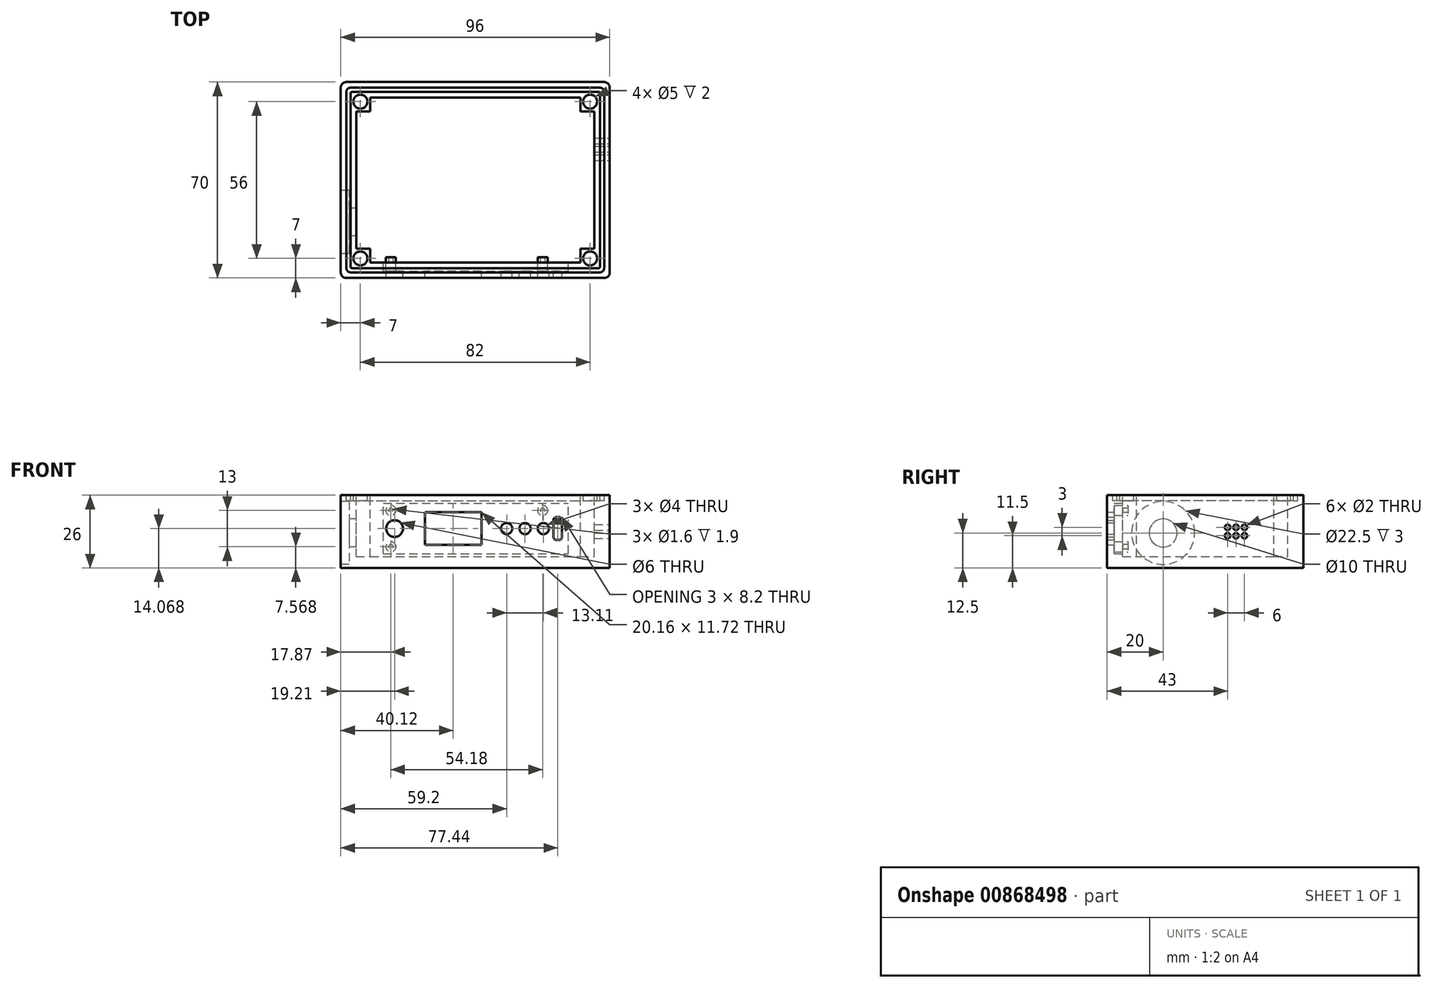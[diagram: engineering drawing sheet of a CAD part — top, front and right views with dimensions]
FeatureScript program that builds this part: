
annotation { "Feature Type Name" : "Feature", "Feature Type Description" : "" }
export const myFeature = defineFeature(function(context is Context, id is Id, definition is map)
    precondition{}
    {
        {
            var Q0;
            Q0=qCreatedBy(makeId("Top.planeOp"),FACE);
            var sketch = newSketch(context, id + "F0", { "sketchPlane" : qUnion([Q0])});
            skLineSegment(sketch, "E0.bottom", {"start": v(-46, 35) * mm, "end": v(46, 35) * mm});
            skLineSegment(sketch, "E0.top", {"start": v(-46, -35) * mm, "end": v(46, -35) * mm});
            skLineSegment(sketch, "E0.left", {"start": v(-48, 33) * mm, "end": v(-48, -33) * mm});
            skLineSegment(sketch, "E0.right", {"start": v(48, 33) * mm, "end": v(48, -33) * mm});
            skPoint(sketch, "E0.middle", {"position": v(0, 0) * mm});
            skPoint(sketch, "E1.visualSharp", {"position": v(-48, 35) * mm});
            skArc(sketch, "E1.filletArc", {"start": v(-46, 35) * mm, "mid": v(-47.41, 34.41) * mm, "end": v(-48, 33) * mm});
            skPoint(sketch, "E2.visualSharp", {"position": v(-48, -35) * mm});
            skArc(sketch, "E2.filletArc", {"start": v(-48, -33) * mm, "mid": v(-47.41, -34.41) * mm, "end": v(-46, -35) * mm});
            skPoint(sketch, "E3.visualSharp", {"position": v(48, -35) * mm});
            skArc(sketch, "E3.filletArc", {"start": v(46, -35) * mm, "mid": v(47.41, -34.41) * mm, "end": v(48, -33) * mm});
            skPoint(sketch, "E4.visualSharp", {"position": v(48, 35) * mm});
            skArc(sketch, "E4.filletArc", {"start": v(48, 33) * mm, "mid": v(47.41, 34.41) * mm, "end": v(46, 35) * mm});
            skSolve(sketch);
        }
        {
            var Q0;
            Q0=makeQuery(id+"F0.imprint","IMPRINT",FACE,{"disambiguationData":[TD([[makeQuery(id+"F0.imprint","IMPRINT",EDGE,{"derivedFrom":sQuery(id+"F0.wireOp",EDGE,"U18dfylj-Norm-gyCY-oxJm-QVkYRqjWbd2D.bottom")}),-1.0]])]});
            var Q1;
            Q1 = qSketchRegion(id + "F0", true);
            extrude(context, id + "F1", {"entities" : qUnion([Q0, Q1]), "depth" : 26 * mm, "offsetDistance" : 25 * mm});
        }
        {
            var Q0;
            Q0=makeQuery(id+"F1.opExtrude","CAP_FACE",FACE,{"disambiguationData":[OSD([sQuery(id+"F0.wireOp",EDGE,"E0.bottom"),sQuery(id+"F0.wireOp",EDGE,"E0.top"),sQuery(id+"F0.wireOp",EDGE,"E0.left"),sQuery(id+"F0.wireOp",EDGE,"E0.right"),sQuery(id+"F0.wireOp",EDGE,"E1.filletArc"),sQuery(id+"F0.wireOp",EDGE,"E2.filletArc"),sQuery(id+"F0.wireOp",EDGE,"E3.filletArc"),sQuery(id+"F0.wireOp",EDGE,"E4.filletArc")])],"isStart":false});
            var sketch = newSketch(context, id + "F2", { "sketchPlane" : qUnion([Q0])});
            skLineSegment(sketch, "E5.bottom", {"start": v(-44.5, 33) * mm, "end": v(44.5, 33) * mm});
            skLineSegment(sketch, "E5.top", {"start": v(-44.5, -33) * mm, "end": v(44.5, -33) * mm});
            skLineSegment(sketch, "E5.left", {"start": v(-46, 31.5) * mm, "end": v(-46, -31.5) * mm});
            skLineSegment(sketch, "E5.right", {"start": v(46, 31.5) * mm, "end": v(46, -31.5) * mm});
            skPoint(sketch, "E5.middle", {"position": v(0, 0) * mm});
            skPoint(sketch, "E6.visualSharp", {"position": v(-46, 33) * mm});
            skArc(sketch, "E6.filletArc", {"start": v(-44.5, 33) * mm, "mid": v(-45.56, 32.56) * mm, "end": v(-46, 31.5) * mm});
            skPoint(sketch, "E7.visualSharp", {"position": v(46, 33) * mm});
            skArc(sketch, "E7.filletArc", {"start": v(46, 31.5) * mm, "mid": v(45.56, 32.56) * mm, "end": v(44.5, 33) * mm});
            skPoint(sketch, "E8.visualSharp", {"position": v(46, -33) * mm});
            skArc(sketch, "E8.filletArc", {"start": v(44.5, -33) * mm, "mid": v(45.56, -32.56) * mm, "end": v(46, -31.5) * mm});
            skPoint(sketch, "E9.visualSharp", {"position": v(-46, -33) * mm});
            skArc(sketch, "E9.filletArc", {"start": v(-46, -31.5) * mm, "mid": v(-45.56, -32.56) * mm, "end": v(-44.5, -33) * mm});
            skLineSegment(sketch, "E10.bottom", {"start": v(-44, 31.5) * mm, "end": v(44, 31.5) * mm});
            skLineSegment(sketch, "E10.top", {"start": v(-44, -31.5) * mm, "end": v(44, -31.5) * mm});
            skLineSegment(sketch, "E10.left", {"start": v(-44.5, 31) * mm, "end": v(-44.5, -31) * mm});
            skLineSegment(sketch, "E10.right", {"start": v(44.5, 31) * mm, "end": v(44.5, -31) * mm});
            skArc(sketch, "E11.filletArc", {"start": v(-44, 31.5) * mm, "mid": v(-44.35, 31.35) * mm, "end": v(-44.5, 31) * mm});
            skArc(sketch, "E12.filletArc", {"start": v(-44.5, -31) * mm, "mid": v(-44.35, -31.35) * mm, "end": v(-44, -31.5) * mm});
            skArc(sketch, "E13.filletArc", {"start": v(44, -31.5) * mm, "mid": v(44.35, -31.35) * mm, "end": v(44.5, -31) * mm});
            skArc(sketch, "E14.filletArc", {"start": v(44.5, 31) * mm, "mid": v(44.35, 31.35) * mm, "end": v(44, 31.5) * mm});
            skSolve(sketch);
        }
        {
            var Q0;
            Q0=makeQuery(id+"F2.imprint","IMPRINT",FACE,{"disambiguationData":[TD([[makeQuery(id+"F2.imprint","IMPRINT",EDGE,{"derivedFrom":sQuery(id+"F2.wireOp",EDGE,"E5.bottom")}),-1.0]])]});
            extrude(context, id + "F3", {"entities" : qUnion([Q0]), "operationType" : NewBodyOperationType.REMOVE, "oppositeDirection" : true, "depth" : 2 * mm, "offsetDistance" : 25 * mm});
        }
        {
            var Q0;
            Q0=makeQuery(id+"F3.boolean.opBoolean","SPLIT",FACE,{"disambiguationData":[TD([makeQuery(id+"F3.opExtrude","SWEPT_FACE",FACE,{"disambiguationData":[OSD([sQuery(id+"F2.wireOp",EDGE,"E10.bottom")])]})])],"derivedFrom":makeQuery(id+"F1.opExtrude","CAP_FACE",FACE,{"disambiguationData":[OSD([sQuery(id+"F0.wireOp",EDGE,"E0.bottom"),sQuery(id+"F0.wireOp",EDGE,"E0.top"),sQuery(id+"F0.wireOp",EDGE,"E0.left"),sQuery(id+"F0.wireOp",EDGE,"E0.right"),sQuery(id+"F0.wireOp",EDGE,"E1.filletArc"),sQuery(id+"F0.wireOp",EDGE,"E2.filletArc"),sQuery(id+"F0.wireOp",EDGE,"E3.filletArc"),sQuery(id+"F0.wireOp",EDGE,"E4.filletArc")])],"isStart":false})});
            var sketch = newSketch(context, id + "F4", { "sketchPlane" : qUnion([Q0])});
            skCircle(sketch, "E15", {"center": v(-41, -28) * mm, "radius": 2.5 * mm});
            skCircle(sketch, "E16", {"center": v(-41, 28) * mm, "radius": 2.5 * mm});
            skCircle(sketch, "E17", {"center": v(41, 28) * mm, "radius": 2.5 * mm});
            skCircle(sketch, "E18", {"center": v(41, -28) * mm, "radius": 2.5 * mm});
            skSolve(sketch);
        }
        {
            var Q0;
            Q0=makeQuery(id+"F4.imprint","IMPRINT",FACE,{"disambiguationData":[TD([[makeQuery(id+"F4.imprint","IMPRINT",EDGE,{"derivedFrom":sQuery(id+"F4.wireOp",EDGE,"E15")}),1.0]])]});
            var Q1;
            Q1=makeQuery(id+"F4.imprint","IMPRINT",FACE,{"disambiguationData":[TD([[makeQuery(id+"F4.imprint","IMPRINT",EDGE,{"derivedFrom":sQuery(id+"F4.wireOp",EDGE,"E16")}),1.0]])]});
            var Q2;
            Q2=makeQuery(id+"F4.imprint","IMPRINT",FACE,{"disambiguationData":[TD([[makeQuery(id+"F4.imprint","IMPRINT",EDGE,{"derivedFrom":sQuery(id+"F4.wireOp",EDGE,"E17")}),1.0]])]});
            var Q3;
            Q3=makeQuery(id+"F4.imprint","IMPRINT",FACE,{"disambiguationData":[TD([[makeQuery(id+"F4.imprint","IMPRINT",EDGE,{"derivedFrom":sQuery(id+"F4.wireOp",EDGE,"E18")}),1.0]])]});
            extrude(context, id + "F5", {"entities" : qUnion([Q0, Q1, Q2, Q3]), "operationType" : NewBodyOperationType.REMOVE, "oppositeDirection" : true, "depth" : 2 * mm, "offsetDistance" : 25 * mm});
        }
        {
            var Q0;
            Q0=makeQuery(id+"F3.boolean.opBoolean","SPLIT",FACE,{"disambiguationData":[TD([makeQuery(id+"F3.opExtrude","SWEPT_FACE",FACE,{"disambiguationData":[OSD([sQuery(id+"F2.wireOp",EDGE,"E10.bottom")])]})])],"derivedFrom":makeQuery(id+"F1.opExtrude","CAP_FACE",FACE,{"disambiguationData":[OSD([sQuery(id+"F0.wireOp",EDGE,"E0.bottom"),sQuery(id+"F0.wireOp",EDGE,"E0.top"),sQuery(id+"F0.wireOp",EDGE,"E0.left"),sQuery(id+"F0.wireOp",EDGE,"E0.right"),sQuery(id+"F0.wireOp",EDGE,"E1.filletArc"),sQuery(id+"F0.wireOp",EDGE,"E2.filletArc"),sQuery(id+"F0.wireOp",EDGE,"E3.filletArc"),sQuery(id+"F0.wireOp",EDGE,"E4.filletArc")])],"isStart":false})});
            var sketch = newSketch(context, id + "F6", { "sketchPlane" : qUnion([Q0])});
            skLineSegment(sketch, "E19.bottom", {"start": v(-42.5, -24.5) * mm, "end": v(42.5, -24.5) * mm});
            skLineSegment(sketch, "E19.top", {"start": v(-42.5, 24.5) * mm, "end": v(42.5, 24.5) * mm});
            skLineSegment(sketch, "E19.left", {"start": v(-42.5, -24.5) * mm, "end": v(-42.5, 24.5) * mm});
            skLineSegment(sketch, "E19.right", {"start": v(42.5, -24.5) * mm, "end": v(42.5, 24.5) * mm});
            skPoint(sketch, "E19.middle", {"position": v(0, 0) * mm});
            skLineSegment(sketch, "E20.bottom", {"start": v(-37.5, -29.5) * mm, "end": v(37.5, -29.5) * mm});
            skLineSegment(sketch, "E20.top", {"start": v(-37.5, 29.5) * mm, "end": v(37.5, 29.5) * mm});
            skLineSegment(sketch, "E20.left", {"start": v(-37.5, -29.5) * mm, "end": v(-37.5, 29.5) * mm});
            skLineSegment(sketch, "E20.right", {"start": v(37.5, -29.5) * mm, "end": v(37.5, 29.5) * mm});
            skSolve(sketch);
        }
        {
            var Q0;
            {var subQ0=sQuery(id+"F6.wireOp",EDGE,"E19.left");Q0=makeQuery(id+"F6.imprint","IMPRINT",FACE,{"disambiguationData":[TD([[makeQuery(id+"F6.imprint","IMPRINT",EDGE,{"derivedFrom":subQ0}),-1.0]])]});}
            var Q1;
            {var subQ5=sQuery(id+"F6.wireOp",EDGE,"E20.bottom");Q1=makeQuery(id+"F6.imprint","IMPRINT",FACE,{"disambiguationData":[TD([[makeQuery(id+"F6.imprint","IMPRINT",EDGE,{"derivedFrom":subQ5}),1.0]])]});}
            var Q2;
            {var subQ0=sQuery(id+"F6.wireOp",EDGE,"E20.left");var subQ1=sQuery(id+"F6.wireOp",EDGE,"E19.bottom");var subQ2=makeQuery(id+"F6.imprint","INTERSECT",VERTEX,{"derivedFrom":[subQ1,subQ0]});Q2=makeQuery(id+"F6.imprint","IMPRINT",FACE,{"disambiguationData":[TD([[makeQuery(id+"F6.imprint","IMPRINT",EDGE,{"disambiguationData":[TD([[subQ2,-1.0]])],"derivedFrom":subQ1}),1.0]])]});}
            var Q3;
            {var subQ5=sQuery(id+"F6.wireOp",EDGE,"E20.top");Q3=makeQuery(id+"F6.imprint","IMPRINT",FACE,{"disambiguationData":[TD([[makeQuery(id+"F6.imprint","IMPRINT",EDGE,{"derivedFrom":subQ5}),-1.0]])]});}
            var Q4;
            {var subQ0=sQuery(id+"F6.wireOp",EDGE,"E19.right");Q4=makeQuery(id+"F6.imprint","IMPRINT",FACE,{"disambiguationData":[TD([[makeQuery(id+"F6.imprint","IMPRINT",EDGE,{"derivedFrom":subQ0}),1.0]])]});}
            extrude(context, id + "F7", {"entities" : qUnion([Q0, Q1, Q2, Q3, Q4]), "operationType" : NewBodyOperationType.REMOVE, "oppositeDirection" : true, "depth" : 22 * mm, "offsetDistance" : 25 * mm});
        }
        {
            var Q0;
            Q0=makeQuery(id+"F1.opExtrude","SWEPT_FACE",FACE,{"disambiguationData":[OSD([sQuery(id+"F0.wireOp",EDGE,"E0.right")])]});
            var sketch = newSketch(context, id + "F8", { "sketchPlane" : qUnion([Q0])});
            skPoint(sketch, "E21.centerSnap0", {"position": v(-33, 13) * mm});
            skCircle(sketch, "E22", {"center": v(8, 14.5) * mm, "radius": 1 * mm});
            skPoint(sketch, "E22.centerSnap0", {"position": v(0, 0) * mm});
            skCircle(sketch, "E23", {"center": v(11, 14.5) * mm, "radius": 1 * mm});
            skCircle(sketch, "E24", {"center": v(14, 14.5) * mm, "radius": 1 * mm});
            skCircle(sketch, "E25", {"center": v(8, 11.5) * mm, "radius": 1 * mm});
            skCircle(sketch, "E26", {"center": v(11, 11.5) * mm, "radius": 1 * mm});
            skCircle(sketch, "E27", {"center": v(14, 11.5) * mm, "radius": 1 * mm});
            skSolve(sketch);
        }
        {
            var Q0;
            Q0=makeQuery(id+"F8.imprint","IMPRINT",FACE,{"disambiguationData":[TD([[makeQuery(id+"F8.imprint","IMPRINT",EDGE,{"derivedFrom":sQuery(id+"F8.wireOp",EDGE,"E22")}),1.0]])]});
            var Q1;
            Q1=makeQuery(id+"F8.imprint","IMPRINT",FACE,{"disambiguationData":[TD([[makeQuery(id+"F8.imprint","IMPRINT",EDGE,{"derivedFrom":sQuery(id+"F8.wireOp",EDGE,"E25")}),1.0]])]});
            var Q2;
            Q2=makeQuery(id+"F8.imprint","IMPRINT",FACE,{"disambiguationData":[TD([[makeQuery(id+"F8.imprint","IMPRINT",EDGE,{"derivedFrom":sQuery(id+"F8.wireOp",EDGE,"E26")}),1.0]])]});
            var Q3;
            Q3=makeQuery(id+"F8.imprint","IMPRINT",FACE,{"disambiguationData":[TD([[makeQuery(id+"F8.imprint","IMPRINT",EDGE,{"derivedFrom":sQuery(id+"F8.wireOp",EDGE,"E23")}),1.0]])]});
            var Q4;
            Q4=makeQuery(id+"F8.imprint","IMPRINT",FACE,{"disambiguationData":[TD([[makeQuery(id+"F8.imprint","IMPRINT",EDGE,{"derivedFrom":sQuery(id+"F8.wireOp",EDGE,"E24")}),1.0]])]});
            var Q5;
            Q5=makeQuery(id+"F8.imprint","IMPRINT",FACE,{"disambiguationData":[TD([[makeQuery(id+"F8.imprint","IMPRINT",EDGE,{"derivedFrom":sQuery(id+"F8.wireOp",EDGE,"E27")}),1.0]])]});
            extrude(context, id + "F9", {"entities" : qUnion([Q0, Q1, Q2, Q3, Q4, Q5]), "operationType" : NewBodyOperationType.REMOVE, "endBound" : BoundingType.UP_TO_NEXT, "oppositeDirection" : true, "depth" : 25 * mm, "offsetDistance" : 25 * mm});
        }
        {
            var Q0;
            Q0=makeQuery(id+"F1.opExtrude","SWEPT_FACE",FACE,{"disambiguationData":[OSD([sQuery(id+"F0.wireOp",EDGE,"E0.left")])]});
            var sketch = newSketch(context, id + "F10", { "sketchPlane" : qUnion([Q0])});
            skCircle(sketch, "E28", {"center": v(15, 12.5) * mm, "radius": 5 * mm});
            skCircle(sketch, "E29", {"center": v(15, 12.5) * mm, "radius": 11.25 * mm});
            skSolve(sketch);
        }
        {
            var Q0;
            Q0=makeQuery(id+"F10.imprint","IMPRINT",FACE,{"disambiguationData":[TD([[makeQuery(id+"F10.imprint","IMPRINT",EDGE,{"derivedFrom":sQuery(id+"F10.wireOp",EDGE,"E28")}),-1.0]])]});
            extrude(context, id + "F11", {"entities" : qUnion([Q0]), "operationType" : NewBodyOperationType.REMOVE, "oppositeDirection" : true, "depth" : 3 * mm, "offsetDistance" : 25 * mm});
        }
        {
            var Q0;
            Q0=makeQuery(id+"F10.imprint","IMPRINT",FACE,{"disambiguationData":[TD([[makeQuery(id+"F10.imprint","IMPRINT",EDGE,{"derivedFrom":sQuery(id+"F10.wireOp",EDGE,"E28")}),1.0]])]});
            extrude(context, id + "F12", {"entities" : qUnion([Q0]), "operationType" : NewBodyOperationType.REMOVE, "endBound" : BoundingType.UP_TO_NEXT, "oppositeDirection" : true, "depth" : 25 * mm, "offsetDistance" : 25 * mm});
        }
        {
            var Q0;
            Q0=makeQuery(id+"F7.boolean.opBoolean","COPY",FACE,{"derivedFrom":makeQuery(id+"F7.opExtrude","SWEPT_FACE",FACE,{"disambiguationData":[OSD([sQuery(id+"F6.wireOp",EDGE,"E20.bottom")])]})});
            var sketch = newSketch(context, id + "F13", { "sketchPlane" : qUnion([Q0])});
            skLineSegment(sketch, "E30.bottom", {"start": v(32.79, 5.07) * mm, "end": v(-33.21, 5.07) * mm});
            skLineSegment(sketch, "E30.top", {"start": v(32.79, 23.07) * mm, "end": v(-33.21, 23.07) * mm});
            skLineSegment(sketch, "E30.left", {"start": v(32.79, 5.07) * mm, "end": v(32.79, 23.07) * mm});
            skLineSegment(sketch, "E30.right", {"start": v(-33.21, 5.07) * mm, "end": v(-33.21, 23.07) * mm});
            skPoint(sketch, "E30.middle", {"position": v(-0.21, 14.07) * mm});
            skPoint(sketch, "E30.middle.positionSnap0", {"position": v(45.84, 14.07) * mm});
            skPoint(sketch, "E30.centerSnap0", {"position": v(45.84, 14.07) * mm});
            skLineSegment(sketch, "E31.bottom", {"start": v(-29.94, 9.97) * mm, "end": v(-28.94, 9.97) * mm});
            skLineSegment(sketch, "E31.top", {"start": v(-29.94, 18.17) * mm, "end": v(-28.94, 18.17) * mm});
            skLineSegment(sketch, "E31.left", {"start": v(-30.94, 10.97) * mm, "end": v(-30.94, 17.17) * mm});
            skLineSegment(sketch, "E31.right", {"start": v(-27.94, 10.97) * mm, "end": v(-27.94, 17.17) * mm});
            skPoint(sketch, "E31.middle", {"position": v(-29.44, 14.07) * mm});
            skPoint(sketch, "E31.middle.positionSnap0", {"position": v(-33.21, 14.07) * mm});
            skPoint(sketch, "E31.centerSnap0", {"position": v(-33.21, 14.07) * mm});
            skPoint(sketch, "E32.visualSharp", {"position": v(-27.94, 18.17) * mm});
            skArc(sketch, "E32.filletArc", {"start": v(-27.94, 17.17) * mm, "mid": v(-28.23, 17.87) * mm, "end": v(-28.94, 18.17) * mm});
            skPoint(sketch, "E33.visualSharp", {"position": v(-27.94, 9.97) * mm});
            skArc(sketch, "E33.filletArc", {"start": v(-28.94, 9.97) * mm, "mid": v(-28.23, 10.26) * mm, "end": v(-27.94, 10.97) * mm});
            skPoint(sketch, "E34.visualSharp", {"position": v(-30.94, 9.97) * mm});
            skArc(sketch, "E34.filletArc", {"start": v(-30.94, 10.97) * mm, "mid": v(-30.65, 10.26) * mm, "end": v(-29.94, 9.97) * mm});
            skPoint(sketch, "E35.visualSharp", {"position": v(-30.94, 18.17) * mm});
            skArc(sketch, "E35.filletArc", {"start": v(-29.94, 18.17) * mm, "mid": v(-30.65, 17.87) * mm, "end": v(-30.94, 17.17) * mm});
            skCircle(sketch, "E36", {"center": v(-24.31, 14.07) * mm, "radius": 2 * mm});
            skCircle(sketch, "E37", {"center": v(-17.76, 14.07) * mm, "radius": 2 * mm});
            skCircle(sketch, "E38", {"center": v(-11.2, 14.07) * mm, "radius": 2 * mm});
            skCircle(sketch, "E39", {"center": v(28.79, 14.07) * mm, "radius": 3 * mm});
            skCircle(sketch, "E40", {"center": v(30.13, 20.57) * mm, "radius": 1.8 * mm});
            skCircle(sketch, "E41", {"center": v(30.13, 20.57) * mm, "radius": 0.8 * mm});
            skCircle(sketch, "E42", {"center": v(30.13, 7.57) * mm, "radius": 1.8 * mm});
            skCircle(sketch, "E43", {"center": v(30.13, 7.57) * mm, "radius": 0.8 * mm});
            skLineSegment(sketch, "E44.bottom", {"start": v(-2.2, 19.93) * mm, "end": v(17.96, 19.93) * mm});
            skLineSegment(sketch, "E44.top", {"start": v(-2.2, 8.2) * mm, "end": v(17.96, 8.2) * mm});
            skLineSegment(sketch, "E44.left", {"start": v(-2.2, 19.93) * mm, "end": v(-2.2, 8.2) * mm});
            skLineSegment(sketch, "E44.right", {"start": v(17.96, 19.93) * mm, "end": v(17.96, 8.2) * mm});
            skPoint(sketch, "E44.middle", {"position": v(7.88, 14.07) * mm});
            skCircle(sketch, "E45", {"center": v(-24.05, 20.57) * mm, "radius": 1.8 * mm});
            skCircle(sketch, "E46", {"center": v(-24.05, 20.57) * mm, "radius": 0.8 * mm});
            skSolve(sketch);
        }
        {
            var Q0;
            Q0=makeQuery(id+"F13.imprint","IMPRINT",FACE,{"disambiguationData":[TD([[makeQuery(id+"F13.imprint","IMPRINT",EDGE,{"derivedFrom":sQuery(id+"F13.wireOp",EDGE,"E44.bottom")}),-1.0]])]});
            var Q1;
            Q1=makeQuery(id+"F13.imprint","IMPRINT",FACE,{"disambiguationData":[TD([[makeQuery(id+"F13.imprint","IMPRINT",EDGE,{"derivedFrom":sQuery(id+"F13.wireOp",EDGE,"E39")}),1.0]])]});
            var Q2;
            Q2=makeQuery(id+"F13.imprint","IMPRINT",FACE,{"disambiguationData":[TD([[makeQuery(id+"F13.imprint","IMPRINT",EDGE,{"derivedFrom":sQuery(id+"F13.wireOp",EDGE,"E38")}),1.0]])]});
            var Q3;
            Q3=makeQuery(id+"F13.imprint","IMPRINT",FACE,{"disambiguationData":[TD([[makeQuery(id+"F13.imprint","IMPRINT",EDGE,{"derivedFrom":sQuery(id+"F13.wireOp",EDGE,"E37")}),1.0]])]});
            var Q4;
            Q4=makeQuery(id+"F13.imprint","IMPRINT",FACE,{"disambiguationData":[TD([[makeQuery(id+"F13.imprint","IMPRINT",EDGE,{"derivedFrom":sQuery(id+"F13.wireOp",EDGE,"E36")}),1.0]])]});
            var Q5;
            Q5=makeQuery(id+"F13.imprint","IMPRINT",FACE,{"disambiguationData":[TD([[makeQuery(id+"F13.imprint","IMPRINT",EDGE,{"derivedFrom":sQuery(id+"F13.wireOp",EDGE,"E31.bottom")}),1.0]])]});
            extrude(context, id + "F14", {"entities" : qUnion([Q0, Q1, Q2, Q3, Q4, Q5]), "operationType" : NewBodyOperationType.REMOVE, "endBound" : BoundingType.UP_TO_NEXT, "oppositeDirection" : true, "depth" : 25 * mm, "offsetDistance" : 25 * mm});
        }
        {
            var Q0;
            Q0=makeQuery(id+"F13.imprint","IMPRINT",FACE,{"disambiguationData":[TD([[makeQuery(id+"F13.imprint","IMPRINT",EDGE,{"derivedFrom":sQuery(id+"F13.wireOp",EDGE,"E30.bottom")}),-1.0]])]});
            extrude(context, id + "F15", {"entities" : qUnion([Q0]), "operationType" : NewBodyOperationType.REMOVE, "oppositeDirection" : true, "depth" : -3 * mm, "offsetDistance" : 25 * mm});
        }
        {
            var Q0;
            Q0=makeQuery(id+"F13.imprint","IMPRINT",FACE,{"disambiguationData":[TD([[makeQuery(id+"F13.imprint","IMPRINT",EDGE,{"derivedFrom":sQuery(id+"F13.wireOp",EDGE,"E30.bottom")}),-1.0]])]});
            extrude(context, id + "F16", {"entities" : qUnion([Q0]), "operationType" : NewBodyOperationType.REMOVE, "oppositeDirection" : true, "depth" : 3 * mm, "offsetDistance" : 25 * mm});
        }
        {
            var Q0;
            Q0=makeQuery(id+"F13.imprint","IMPRINT",FACE,{"disambiguationData":[TD([[makeQuery(id+"F13.imprint","IMPRINT",EDGE,{"derivedFrom":sQuery(id+"F13.wireOp",EDGE,"E40")}),1.0]])]});
            var Q1;
            Q1=sQuery(id+"F13.wireOp",EDGE,"E41");
            var Q2;
            Q2=sQuery(id+"F13.wireOp",EDGE,"E40");
            extrude(context, id + "F17", {"entities" : qUnion([Q0]), "operationType" : NewBodyOperationType.ADD, "surfaceEntities" : qUnion([Q1, Q2]), "depth" : 1.9 * mm, "offsetDistance" : 25 * mm});
        }
        {
            var Q0;
            Q0=makeQuery(id+"F13.imprint","IMPRINT",FACE,{"disambiguationData":[TD([[makeQuery(id+"F13.imprint","IMPRINT",EDGE,{"derivedFrom":sQuery(id+"F13.wireOp",EDGE,"E42")}),1.0]])]});
            var Q1;
            Q1=sQuery(id+"F13.wireOp",EDGE,"E43");
            var Q2;
            Q2=sQuery(id+"F13.wireOp",EDGE,"E42");
            extrude(context, id + "F18", {"entities" : qUnion([Q0]), "operationType" : NewBodyOperationType.ADD, "surfaceEntities" : qUnion([Q1, Q2]), "depth" : 1.9 * mm, "offsetDistance" : 25 * mm});
        }
        {
            var Q0;
            Q0=makeQuery(id+"F13.imprint","IMPRINT",FACE,{"disambiguationData":[TD([[makeQuery(id+"F13.imprint","IMPRINT",EDGE,{"derivedFrom":sQuery(id+"F13.wireOp",EDGE,"E45")}),1.0]])]});
            extrude(context, id + "F19", {"entities" : qUnion([Q0]), "operationType" : NewBodyOperationType.ADD, "depth" : 1.9 * mm, "offsetDistance" : 25 * mm});
        }
    });
